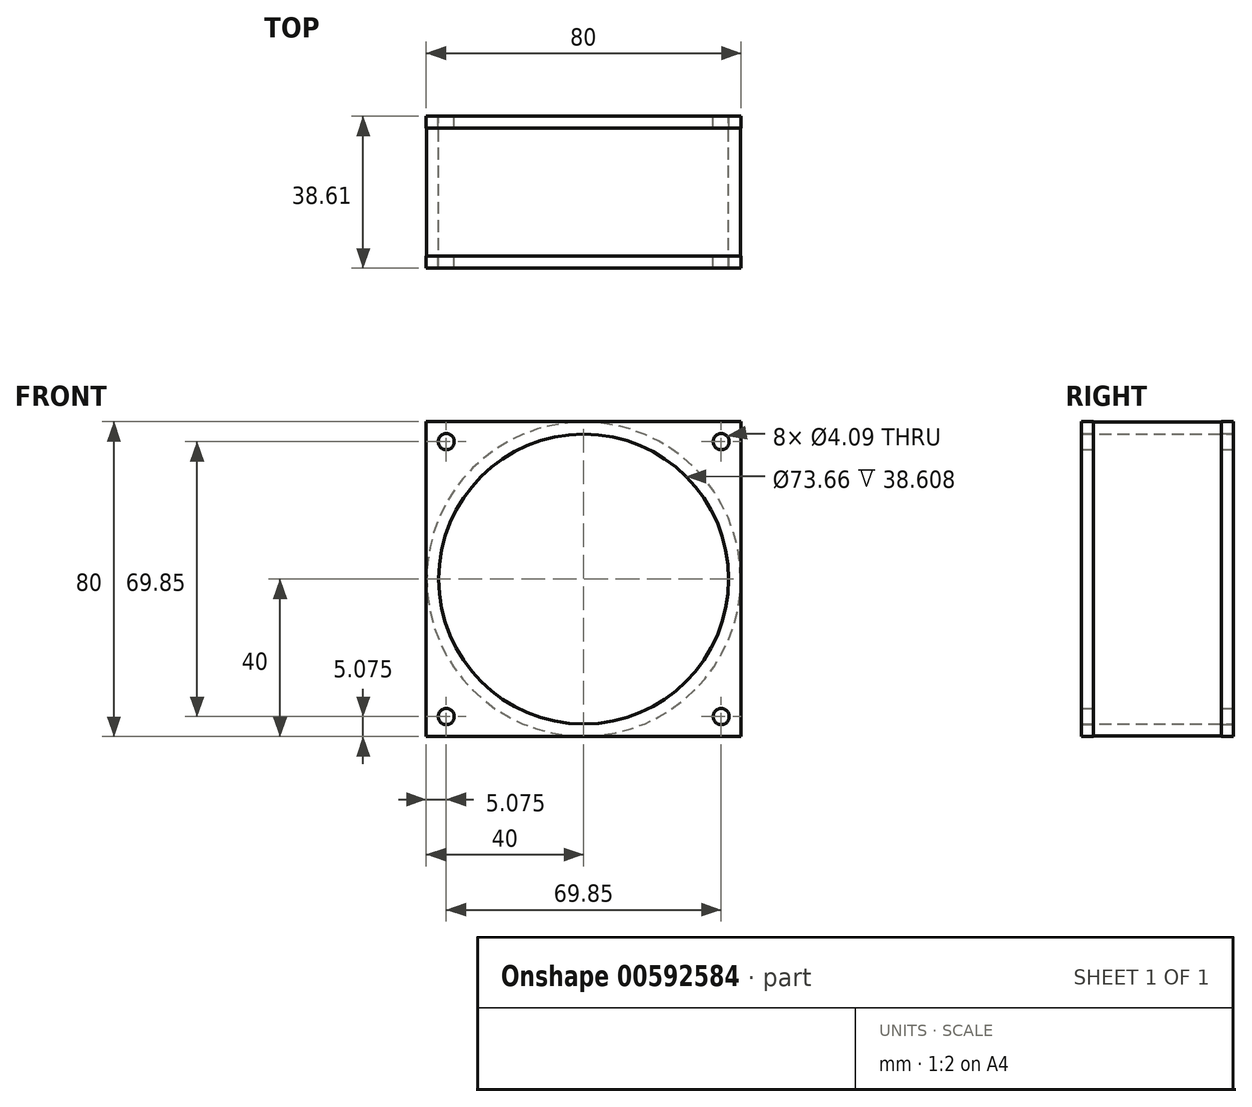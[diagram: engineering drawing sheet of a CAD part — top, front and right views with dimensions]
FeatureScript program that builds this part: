
annotation { "Feature Type Name" : "Feature", "Feature Type Description" : "" }
export const myFeature = defineFeature(function(context is Context, id is Id, definition is map)
    precondition{}
    {
        {
            var Q0;
            Q0=qCreatedBy(makeId("Front.planeOp"),FACE);
            var sketch = newSketch(context, id + "F0", { "sketchPlane" : qUnion([Q0])});
            skLineSegment(sketch, "E0.bottom", {"start": v(-40, 40) * mm, "end": v(40, 40) * mm});
            skLineSegment(sketch, "E0.top", {"start": v(-40, -40) * mm, "end": v(40, -40) * mm});
            skLineSegment(sketch, "E0.left", {"start": v(-40, 40) * mm, "end": v(-40, -40) * mm});
            skLineSegment(sketch, "E0.right", {"start": v(40, 40) * mm, "end": v(40, -40) * mm});
            skPoint(sketch, "E0.middle", {"position": v(0, 0) * mm});
            skLineSegment(sketch, "E1.bottom", {"start": v(-34.92, 34.92) * mm, "end": v(34.93, 34.92) * mm, "construction": true});
            skLineSegment(sketch, "E1.top", {"start": v(-34.92, -34.92) * mm, "end": v(34.92, -34.92) * mm, "construction": true});
            skLineSegment(sketch, "E1.left", {"start": v(-34.93, 34.92) * mm, "end": v(-34.93, -34.92) * mm, "construction": true});
            skLineSegment(sketch, "E1.right", {"start": v(34.92, 34.92) * mm, "end": v(34.92, -34.92) * mm, "construction": true});
            skCircle(sketch, "E2", {"center": v(-34.92, 34.93) * mm, "radius": 2.04 * mm});
            skCircle(sketch, "E3", {"center": v(34.93, 34.93) * mm, "radius": 2.04 * mm});
            skCircle(sketch, "E4", {"center": v(-34.93, -34.93) * mm, "radius": 2.04 * mm});
            skCircle(sketch, "E5", {"center": v(34.92, -34.93) * mm, "radius": 2.04 * mm});
            skLineSegment(sketch, "E6", {"start": v(24.63, 38.23) * mm, "end": v(38.23, 24.63) * mm});
            skLineSegment(sketch, "E7", {"start": v(-38.23, -24.63) * mm, "end": v(-24.63, -38.23) * mm});
            skLineSegment(sketch, "E8", {"start": v(-40, -40) * mm, "end": v(-31.43, -31.43) * mm, "construction": true});
            skLineSegment(sketch, "E9", {"start": v(-31.43, -31.43) * mm, "end": v(31.43, 31.43) * mm, "construction": true});
            skLineSegment(sketch, "E10.0", {"start": v(-38.23, 38.23) * mm, "end": v(38.23, 38.23) * mm});
            skLineSegment(sketch, "E10.1", {"start": v(-38.23, 38.23) * mm, "end": v(-38.23, -38.23) * mm});
            skLineSegment(sketch, "E10.2", {"start": v(-38.23, -38.23) * mm, "end": v(38.23, -38.23) * mm});
            skLineSegment(sketch, "E10.3", {"start": v(38.23, 38.23) * mm, "end": v(38.23, -38.23) * mm});
            skLineSegment(sketch, "E11", {"start": v(-38.23, 24.63) * mm, "end": v(-24.63, 38.23) * mm});
            skLineSegment(sketch, "E12", {"start": v(24.63, -38.23) * mm, "end": v(38.23, -24.63) * mm});
            skCircle(sketch, "E13", {"center": v(0, 0) * mm, "radius": 39.88 * mm});
            skCircle(sketch, "E14.0", {"center": v(0, 0) * mm, "radius": 36.83 * mm});
            skSolve(sketch);
        }
        {
            var Q0;
            Q0=makeQuery(id+"F0.imprint","IMPRINT",FACE,{"disambiguationData":[TD([[makeQuery(id+"F0.imprint","IMPRINT",EDGE,{"derivedFrom":sQuery(id+"F0.wireOp",EDGE,"E0.bottom")}),-1.0]])]});
            var Q1;
            Q1=makeQuery(id+"F0.imprint","IMPRINT",FACE,{"disambiguationData":[TD([[makeQuery(id+"F0.imprint","IMPRINT",EDGE,{"derivedFrom":sQuery(id+"F0.wireOp",EDGE,"E3")}),-1.0]])]});
            var Q2;
            Q2=makeQuery(id+"F0.imprint","IMPRINT",FACE,{"disambiguationData":[TD([[makeQuery(id+"F0.imprint","IMPRINT",EDGE,{"derivedFrom":sQuery(id+"F0.wireOp",EDGE,"E5")}),-1.0]])]});
            var Q3;
            Q3=makeQuery(id+"F0.imprint","IMPRINT",FACE,{"disambiguationData":[TD([[makeQuery(id+"F0.imprint","IMPRINT",EDGE,{"derivedFrom":sQuery(id+"F0.wireOp",EDGE,"E4")}),-1.0]])]});
            var Q4;
            Q4=makeQuery(id+"F0.imprint","IMPRINT",FACE,{"disambiguationData":[TD([[makeQuery(id+"F0.imprint","IMPRINT",EDGE,{"derivedFrom":sQuery(id+"F0.wireOp",EDGE,"E2")}),-1.0]])]});
            var Q5;
            {var subQ0=sQuery(id+"F0.wireOp",EDGE,"E13");var subQ1=sQuery(id+"F0.wireOp",EDGE,"E10.0");var subQ2=makeQuery(id+"F0.imprint","INTERSECT",VERTEX,{"disambiguationData":[OD(0.0)],"derivedFrom":[subQ1,subQ0]});Q5=makeQuery(id+"F0.imprint","IMPRINT",FACE,{"disambiguationData":[TD([[makeQuery(id+"F0.imprint","IMPRINT",EDGE,{"disambiguationData":[TD([[subQ2,-1.0]])],"derivedFrom":subQ1}),1.0]])]});}
            var Q6;
            {var subQ0=sQuery(id+"F0.wireOp",EDGE,"E13");var subQ1=sQuery(id+"F0.wireOp",EDGE,"E10.3");var subQ2=makeQuery(id+"F0.imprint","INTERSECT",VERTEX,{"disambiguationData":[OD(0.0)],"derivedFrom":[subQ1,subQ0]});Q6=makeQuery(id+"F0.imprint","IMPRINT",FACE,{"disambiguationData":[TD([[makeQuery(id+"F0.imprint","IMPRINT",EDGE,{"disambiguationData":[TD([[subQ2,-1.0]])],"derivedFrom":subQ1}),1.0]])]});}
            var Q7;
            {var subQ0=sQuery(id+"F0.wireOp",EDGE,"E13");var subQ1=sQuery(id+"F0.wireOp",EDGE,"E10.2");var subQ2=makeQuery(id+"F0.imprint","INTERSECT",VERTEX,{"disambiguationData":[OD(0.0)],"derivedFrom":[subQ1,subQ0]});Q7=makeQuery(id+"F0.imprint","IMPRINT",FACE,{"disambiguationData":[TD([[makeQuery(id+"F0.imprint","IMPRINT",EDGE,{"disambiguationData":[TD([[subQ2,-1.0]])],"derivedFrom":subQ1}),-1.0]])]});}
            var Q8;
            {var subQ0=sQuery(id+"F0.wireOp",EDGE,"E13");var subQ1=sQuery(id+"F0.wireOp",EDGE,"E10.1");var subQ2=makeQuery(id+"F0.imprint","INTERSECT",VERTEX,{"disambiguationData":[OD(0.0)],"derivedFrom":[subQ1,subQ0]});Q8=makeQuery(id+"F0.imprint","IMPRINT",FACE,{"disambiguationData":[TD([[makeQuery(id+"F0.imprint","IMPRINT",EDGE,{"disambiguationData":[TD([[subQ2,-1.0]])],"derivedFrom":subQ1}),-1.0]])]});}
            var Q9;
            {var subQ0=sQuery(id+"F0.wireOp",EDGE,"E7");Q9=makeQuery(id+"F0.imprint","IMPRINT",FACE,{"disambiguationData":[TD([[makeQuery(id+"F0.imprint","IMPRINT",EDGE,{"derivedFrom":subQ0}),1.0]])]});}
            var Q10;
            {var subQ0=sQuery(id+"F0.wireOp",EDGE,"E11");Q10=makeQuery(id+"F0.imprint","IMPRINT",FACE,{"disambiguationData":[TD([[makeQuery(id+"F0.imprint","IMPRINT",EDGE,{"derivedFrom":subQ0}),-1.0]])]});}
            var Q11;
            {var subQ0=sQuery(id+"F0.wireOp",EDGE,"E6");Q11=makeQuery(id+"F0.imprint","IMPRINT",FACE,{"disambiguationData":[TD([[makeQuery(id+"F0.imprint","IMPRINT",EDGE,{"derivedFrom":subQ0}),-1.0]])]});}
            var Q12;
            {var subQ0=sQuery(id+"F0.wireOp",EDGE,"E12");Q12=makeQuery(id+"F0.imprint","IMPRINT",FACE,{"disambiguationData":[TD([[makeQuery(id+"F0.imprint","IMPRINT",EDGE,{"derivedFrom":subQ0}),1.0]])]});}
            extrude(context, id + "F1", {"entities" : qUnion([Q0, Q1, Q2, Q3, Q4, Q5, Q6, Q7, Q8, Q9, Q10, Q11, Q12]), "depth" : 3.05 * mm, "offsetDistance" : 25.4 * mm});
        }
        {
            var Q0;
            Q0=makeQuery(id+"F0.imprint","IMPRINT",FACE,{"disambiguationData":[TD([[makeQuery(id+"F0.imprint","IMPRINT",EDGE,{"derivedFrom":sQuery(id+"F0.wireOp",EDGE,"E14.0")}),-1.0]])]});
            var Q1;
            {var subQ0=sQuery(id+"F0.wireOp",EDGE,"E13");var subQ1=sQuery(id+"F0.wireOp",EDGE,"E10.3");var subQ2=makeQuery(id+"F0.imprint","INTERSECT",VERTEX,{"disambiguationData":[OD(0.0)],"derivedFrom":[subQ1,subQ0]});Q1=makeQuery(id+"F0.imprint","IMPRINT",FACE,{"disambiguationData":[TD([[makeQuery(id+"F0.imprint","IMPRINT",EDGE,{"disambiguationData":[TD([[subQ2,-1.0]])],"derivedFrom":subQ1}),1.0]])]});}
            var Q2;
            {var subQ0=sQuery(id+"F0.wireOp",EDGE,"E13");var subQ1=sQuery(id+"F0.wireOp",EDGE,"E10.1");var subQ2=makeQuery(id+"F0.imprint","INTERSECT",VERTEX,{"disambiguationData":[OD(0.0)],"derivedFrom":[subQ1,subQ0]});Q2=makeQuery(id+"F0.imprint","IMPRINT",FACE,{"disambiguationData":[TD([[makeQuery(id+"F0.imprint","IMPRINT",EDGE,{"disambiguationData":[TD([[subQ2,-1.0]])],"derivedFrom":subQ1}),-1.0]])]});}
            var Q3;
            {var subQ0=sQuery(id+"F0.wireOp",EDGE,"E13");var subQ1=sQuery(id+"F0.wireOp",EDGE,"E10.2");var subQ2=makeQuery(id+"F0.imprint","INTERSECT",VERTEX,{"disambiguationData":[OD(0.0)],"derivedFrom":[subQ1,subQ0]});Q3=makeQuery(id+"F0.imprint","IMPRINT",FACE,{"disambiguationData":[TD([[makeQuery(id+"F0.imprint","IMPRINT",EDGE,{"disambiguationData":[TD([[subQ2,-1.0]])],"derivedFrom":subQ1}),-1.0]])]});}
            var Q4;
            {var subQ0=sQuery(id+"F0.wireOp",EDGE,"E13");var subQ1=sQuery(id+"F0.wireOp",EDGE,"E10.0");var subQ2=makeQuery(id+"F0.imprint","INTERSECT",VERTEX,{"disambiguationData":[OD(0.0)],"derivedFrom":[subQ1,subQ0]});Q4=makeQuery(id+"F0.imprint","IMPRINT",FACE,{"disambiguationData":[TD([[makeQuery(id+"F0.imprint","IMPRINT",EDGE,{"disambiguationData":[TD([[subQ2,-1.0]])],"derivedFrom":subQ1}),1.0]])]});}
            extrude(context, id + "F2", {"entities" : qUnion([Q0, Q1, Q2, Q3, Q4]), "operationType" : NewBodyOperationType.ADD, "depth" : 35.56 * mm, "offsetDistance" : 25.4 * mm});
        }
        {
            var Q0;
            Q0=makeQuery(id+"F2.opExtrude","CAP_FACE",FACE,{"disambiguationData":[OSD([sQuery(id+"F0.wireOp",EDGE,"E13"),sQuery(id+"F0.wireOp",EDGE,"E14.0")])],"isStart":false});
            var sketch = newSketch(context, id + "F3", { "sketchPlane" : qUnion([Q0])});
            skLineSegment(sketch, "E15.0", {"start": v(-40, 40) * mm, "end": v(-40, -40) * mm});
            skLineSegment(sketch, "E16.0", {"start": v(-40, -40) * mm, "end": v(40, -40) * mm});
            skCircle(sketch, "E17.0", {"center": v(-34.93, -34.93) * mm, "radius": 2.04 * mm});
            skLineSegment(sketch, "E18.0", {"start": v(-38.23, -24.63) * mm, "end": v(-24.63, -38.23) * mm});
            skLineSegment(sketch, "E19.0", {"start": v(-38.23, -38.23) * mm, "end": v(38.23, -38.23) * mm});
            skLineSegment(sketch, "E20.0", {"start": v(-38.23, 38.23) * mm, "end": v(-38.23, -38.23) * mm});
            skLineSegment(sketch, "E21.0", {"start": v(-38.23, 38.23) * mm, "end": v(38.23, 38.23) * mm});
            skLineSegment(sketch, "E22.0", {"start": v(-38.23, 24.63) * mm, "end": v(-24.63, 38.23) * mm});
            skCircle(sketch, "E23.0", {"center": v(-34.92, 34.93) * mm, "radius": 2.04 * mm});
            skLineSegment(sketch, "E24.0", {"start": v(-40, 40) * mm, "end": v(40, 40) * mm});
            skCircle(sketch, "E25.0", {"center": v(34.93, 34.93) * mm, "radius": 2.04 * mm});
            skLineSegment(sketch, "E26.0", {"start": v(24.63, 38.23) * mm, "end": v(38.23, 24.63) * mm});
            skLineSegment(sketch, "E27.0", {"start": v(38.23, 38.23) * mm, "end": v(38.23, -38.23) * mm});
            skLineSegment(sketch, "E28.0", {"start": v(40, 40) * mm, "end": v(40, -40) * mm});
            skLineSegment(sketch, "E29.0", {"start": v(24.63, -38.23) * mm, "end": v(38.23, -24.63) * mm});
            skCircle(sketch, "E30.0", {"center": v(34.92, -34.93) * mm, "radius": 2.04 * mm});
            skSolve(sketch);
        }
        {
            var Q0;
            Q0 = qSketchRegion(id + "F3", true);
            var Q1;
            Q1=makeQuery(id+"F3.imprint","IMPRINT",FACE,{"disambiguationData":[TD([[makeQuery(id+"F3.imprint","IMPRINT",EDGE,{"derivedFrom":sQuery(id+"F3.wireOp",EDGE,"E17.0")}),-1.0]])]});
            var Q2;
            {var subQ3=sQuery(id+"F3.wireOp",EDGE,"E22.0");Q2=makeQuery(id+"F3.imprint","IMPRINT",FACE,{"disambiguationData":[TD([[makeQuery(id+"F3.imprint","IMPRINT",EDGE,{"derivedFrom":subQ3}),1.0]])]});}
            var Q3;
            Q3=makeQuery(id+"F3.imprint","IMPRINT",FACE,{"disambiguationData":[TD([[makeQuery(id+"F3.imprint","IMPRINT",EDGE,{"derivedFrom":sQuery(id+"F3.wireOp",EDGE,"E25.0")}),-1.0]])]});
            var Q4;
            {var subQ3=sQuery(id+"F3.wireOp",EDGE,"E29.0");Q4=makeQuery(id+"F3.imprint","IMPRINT",FACE,{"disambiguationData":[TD([[makeQuery(id+"F3.imprint","IMPRINT",EDGE,{"derivedFrom":subQ3}),-1.0]])]});}
            var Q5;
            Q5=makeQuery(id+"F3.imprint","IMPRINT",FACE,{"disambiguationData":[TD([[makeQuery(id+"F3.imprint","IMPRINT",EDGE,{"derivedFrom":makeQuery(id+"F2.opExtrude","CAP_EDGE",EDGE,{"disambiguationData":[OSD([sQuery(id+"F0.wireOp",EDGE,"E14.0")])],"isStart":false})}),-1.0]])]});
            var Q6;
            {var subQ0=sQuery(id+"F3.wireOp",EDGE,"E29.0");Q6=makeQuery(id+"F3.imprint","IMPRINT",FACE,{"disambiguationData":[TD([[makeQuery(id+"F3.imprint","IMPRINT",EDGE,{"derivedFrom":subQ0}),1.0]])]});}
            var Q7;
            {var subQ0=sQuery(id+"F3.wireOp",EDGE,"E26.0");Q7=makeQuery(id+"F3.imprint","IMPRINT",FACE,{"disambiguationData":[TD([[makeQuery(id+"F3.imprint","IMPRINT",EDGE,{"derivedFrom":subQ0}),-1.0]])]});}
            var Q8;
            {var subQ0=sQuery(id+"F3.wireOp",EDGE,"E22.0");Q8=makeQuery(id+"F3.imprint","IMPRINT",FACE,{"disambiguationData":[TD([[makeQuery(id+"F3.imprint","IMPRINT",EDGE,{"derivedFrom":subQ0}),-1.0]])]});}
            var Q9;
            {var subQ0=sQuery(id+"F3.wireOp",EDGE,"E18.0");Q9=makeQuery(id+"F3.imprint","IMPRINT",FACE,{"disambiguationData":[TD([[makeQuery(id+"F3.imprint","IMPRINT",EDGE,{"derivedFrom":subQ0}),1.0]])]});}
            extrude(context, id + "F4", {"entities" : qUnion([Q0, Q1, Q2, Q3, Q4, Q5, Q6, Q7, Q8, Q9]), "operationType" : NewBodyOperationType.ADD, "depth" : 3.05 * mm, "offsetDistance" : 25.4 * mm});
        }
    });
